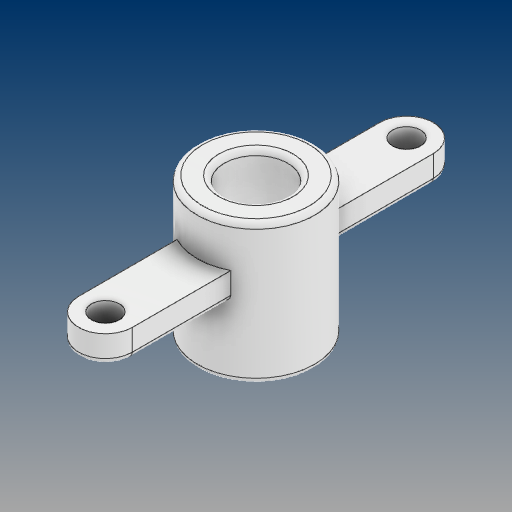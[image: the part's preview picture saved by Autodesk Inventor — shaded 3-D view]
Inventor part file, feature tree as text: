
AUTODESK INVENTOR PART (.ipt)
format: ipt  version: 2021 (Build 250183000, 183)  size: 210,432 bytes
history: native  units: mm
features: extrude x6, sketch x5, fillet x2, hole x1, chamfer x1, projected_geometry x1
ambient origin geometry x8: Origin, YZ Plane, XZ Plane, XY Plane, X Axis, Y Axis, Z Axis, Center Point
bodies: Solid1 (feature_tree)
feature tree (16):
  sketch  "Sketch1"  dims[d0=56.0mm d1=5.0mm]
  extrude  "Extrusion1"  Depth=5.0mm
  extrude  "Extrusion2"  Depth=5.0mm
  extrude  "Extrusion3"  Depth=5.0mm TaperAngle=0.0deg
  hole  "Hole1"  [1 undecoded]
  extrude  "Extrusion4"  Depth=28.0mm TaperAngle=0.0deg
  extrude  "Extrusion5"  Depth=10.0mm TaperAngle=0.0deg
  extrude  "Extrusion6"  Depth=1.0mm
  fillet  "Fillet1"  Radius=3.0mm
  fillet  "Fillet2"  Radius=1.0mm
  chamfer  "Chamfer1"  Distance=1.0mm
  sketch  "Sketch2"  dims[d2=11.8mm d3=5.0mm]
  projected_geometry  "Projected Loop1"
  sketch  "Sketch3"  dims[d4=5.0mm d5=0.0mm d6=18.25mm d7=0.0mm]
  sketch  "Sketch4"  dims[d8=8.0mm d9=0.0mm d10=7.0mm]
  sketch  "Sketch5"  dims[d11=5.2mm d12=6.0mm d13=4.0mm d14=2.0mm d15=90.0deg d16=8.0mm d17=20.594885mm d19=28.0mm d20=0.0mm d21=10.0mm d22=0.0mm d23=6.5mm d24=3.0mm d25=0.0mm d26=1.0mm d27=1.0mm d28=0.5mm d29=2.0mm d30=45.0deg]
note: 1 required parameter value undecoded (feature->parameter linkage not recoverable at this tier; creation-order binding heuristic only, values carry confidence <= 0.55)
